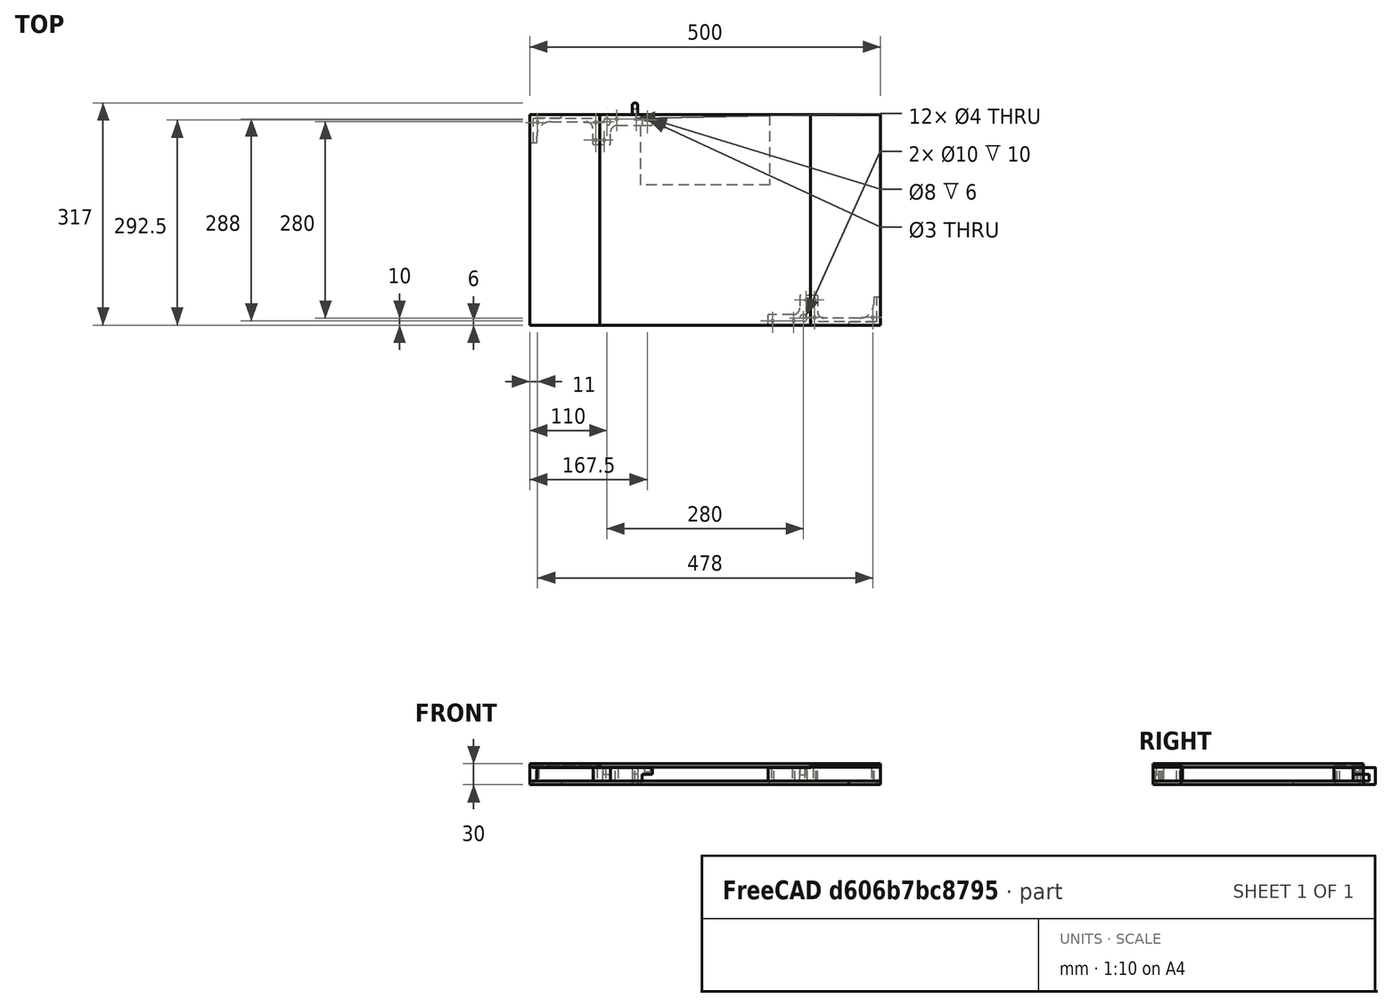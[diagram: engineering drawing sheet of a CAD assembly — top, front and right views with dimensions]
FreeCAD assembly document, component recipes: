
FREECAD ASSEMBLY — COMPONENT RECIPES ("ChessBoard")

This assembly document has 9 components, labeled P0..P8 below (a component is one placed body or linked part). 6 of them carry a construction recipe — the FreeCAD feature program that regenerates the part from scratch, quoted from this document or its linked companion documents; the rest are supplied as boundary geometry only. No exploded tour is included for this assembly.
COMPONENT P0 — recipe-attached ("Bottom", modeled in this document).
Construction recipe (the document's own serialized feature program — sketch geometry with constraints, then the solid features built on it; lengths are millimeters unless a unit is written):

FEATURE [Sketcher::SketchObject] Sketch
  ArcFitTolerance = 1e-06
  AttachmentSupport = -> [XY_Plane]
  FullyConstrained = true
  MakeInternals = false
  MapMode = 5
  sketch-geometry (5):
    g0: LineSegment StartX=-250 StartY=-150 StartZ=0 EndX=250 EndY=-150 EndZ=0
    g1: LineSegment StartX=250 StartY=-150 StartZ=0 EndX=250 EndY=150 EndZ=0
    g2: LineSegment StartX=250 StartY=150 StartZ=0 EndX=-250 EndY=150 EndZ=0
    g3: LineSegment StartX=-250 StartY=150 StartZ=0 EndX=-250 EndY=-150 EndZ=0
    g4: GeomPoint [constr] X=0 Y=0 Z=0
  constraints (12):
    c: Coincident(g0,g1)
    c: Coincident(g1,g2)
    c: Coincident(g2,g3)
    c: Coincident(g3,g0)
    c: Horizontal(g0)
    c: Horizontal(g2)
    c: Vertical(g1)
    c: Vertical(g3)
    c: Symmetric(g2,g0,g4)
    c: Distance(g1,g3) = 500
    c: Distance(g0,g2) = 300
    c: Coincident(g4,g-1)
FEATURE [PartDesign::Pad] Pad
  Direction = (0,0,1)
  Length = 5
  Length2 = 10
  Profile = -> Sketch
  ReferenceAxis = -> Sketch [N_Axis]
  Refine = true
  Suppressed = false
  Type = 0
FEATURE [Sketcher::SketchObject] Sketch005
  ArcFitTolerance = 1e-06
  AttachmentSupport = -> [Pad]
  ExternalGeometry = -> [Sketch]
  FullyConstrained = false
  MakeInternals = false
  MapMode = 5
  Placement = pos=(0,0,0) rot=(1,0,0;3.14159rad)
  sketch-geometry (4):
    g0: LineSegment StartX=-92 StartY=-50 StartZ=0 EndX=-92 EndY=-193.39 EndZ=0
    g1: LineSegment StartX=-92 StartY=-193.39 StartZ=0 EndX=92 EndY=-193.39 EndZ=0
    g2: LineSegment StartX=92 StartY=-193.39 StartZ=0 EndX=92 EndY=-50 EndZ=0
    g3: LineSegment StartX=92 StartY=-50 StartZ=0 EndX=-92 EndY=-50 EndZ=0
  constraints (11):
    c: Coincident(g0,g1)
    c: Coincident(g1,g2)
    c: Coincident(g2,g3)
    c: Coincident(g3,g0)
    c: Vertical(g0)
    c: Vertical(g2)
    c: Horizontal(g1)
    c: Horizontal(g3)
    c: Distance(g-2,g2) = 92
    c: Distance(g-2,g0) = 92
    c: Distance(g-3,g3) = 100
FEATURE [PartDesign::Pocket] Pocket
  BaseFeature = -> Pad
  Direction = (0,0,1)
  Length = 5
  Length2 = 5
  Profile = -> Sketch005
  ReferenceAxis = -> Sketch005 [N_Axis]
  Refine = true
  Suppressed = false
  Type = 0
FEATURE [PartDesign::Body] Body  label="Bottom"
  AllowCompound = false
  Group = -> [Sketch,Pad,Sketch005,Pocket]
  Origin = -> Origin
  Tip = -> Pocket
COMPONENT P1 — recipe-attached ("MainBoard", modeled in this document).
Construction recipe (the document's own serialized feature program — sketch geometry with constraints, then the solid features built on it; lengths are millimeters unless a unit is written):

FEATURE [Sketcher::SketchObject] Sketch001
  ArcFitTolerance = 1e-06
  AttachmentSupport = -> [XY_Plane001]
  FullyConstrained = true
  MakeInternals = false
  MapMode = 5
  sketch-geometry (5):
    g0: LineSegment StartX=-150 StartY=-150 StartZ=0 EndX=150 EndY=-150 EndZ=0
    g1: LineSegment StartX=150 StartY=-150 StartZ=0 EndX=150 EndY=150 EndZ=0
    g2: LineSegment StartX=150 StartY=150 StartZ=0 EndX=-150 EndY=150 EndZ=0
    g3: LineSegment StartX=-150 StartY=150 StartZ=0 EndX=-150 EndY=-150 EndZ=0
    g4: GeomPoint [constr] X=0 Y=0 Z=0
  constraints (12):
    c: Coincident(g0,g1)
    c: Coincident(g1,g2)
    c: Coincident(g2,g3)
    c: Coincident(g3,g0)
    c: Horizontal(g0)
    c: Horizontal(g2)
    c: Vertical(g1)
    c: Vertical(g3)
    c: Symmetric(g2,g0,g4)
    c: Distance(g1,g3) = 300
    c: Distance(g0,g2) = 300
    c: Coincident(g4,g-1)
FEATURE [PartDesign::Pad] Pad001
  Direction = (0,0,1)
  Length = 5
  Length2 = 10
  Profile = -> Sketch001
  ReferenceAxis = -> Sketch001 [N_Axis]
  Refine = true
  Suppressed = false
  Type = 0
FEATURE [PartDesign::Body] Body001  label="MainBoard"
  AllowCompound = false
  Group = -> [Sketch001,Pad001]
  Origin = -> Origin001
  Placement = pos=(0,0,25) rot=(0,0,1;0rad)
  Tip = -> Pad001
COMPONENT P2 — recipe-attached ("DropLeft", modeled in this document).
Construction recipe (the document's own serialized feature program — sketch geometry with constraints, then the solid features built on it; lengths are millimeters unless a unit is written):

FEATURE [Sketcher::SketchObject] Sketch002
  ArcFitTolerance = 1e-06
  AttachmentSupport = -> [XY_Plane002]
  FullyConstrained = true
  MakeInternals = false
  MapMode = 5
  sketch-geometry (4):
    g0: LineSegment StartX=0 StartY=0 StartZ=0 EndX=0 EndY=-300 EndZ=0
    g1: LineSegment StartX=0 StartY=-300 StartZ=0 EndX=100 EndY=-300 EndZ=0
    g2: LineSegment StartX=100 StartY=-300 StartZ=0 EndX=100 EndY=0 EndZ=0
    g3: LineSegment StartX=100 StartY=0 StartZ=0 EndX=0 EndY=0 EndZ=0
  constraints (11):
    c: Coincident(g0,g1)
    c: Coincident(g1,g2)
    c: Coincident(g2,g3)
    c: Coincident(g3,g0)
    c: Vertical(g0)
    c: Vertical(g2)
    c: Horizontal(g1)
    c: Horizontal(g3)
    c: Distance(g0,g2) = 100
    c: Distance(g1,g3) = 300
    c: Coincident(g0,g-1)
FEATURE [PartDesign::Pad] Pad002
  Direction = (0,0,1)
  Length = 5
  Length2 = 10
  Profile = -> Sketch002
  ReferenceAxis = -> Sketch002 [N_Axis]
  Refine = true
  Suppressed = false
  Type = 0
FEATURE [PartDesign::Body] Body002  label="DropLeft"
  AllowCompound = false
  Group = -> [Sketch002,Pad002]
  Origin = -> Origin002
  Placement = pos=(-250,150,25) rot=(0,0,1;0rad)
  Tip = -> Pad002
COMPONENT P3 — recipe-attached ("DropRight", modeled in this document).
Construction recipe (the document's own serialized feature program — sketch geometry with constraints, then the solid features built on it; lengths are millimeters unless a unit is written):

FEATURE [Sketcher::SketchObject] Sketch003
  ArcFitTolerance = 1e-06
  AttachmentSupport = -> [XY_Plane003]
  FullyConstrained = true
  MakeInternals = false
  MapMode = 5
  sketch-geometry (4):
    g0: LineSegment StartX=0 StartY=0 StartZ=0 EndX=-100 EndY=0 EndZ=0
    g1: LineSegment StartX=-100 StartY=0 StartZ=0 EndX=-100 EndY=-300 EndZ=0
    g2: LineSegment StartX=-100 StartY=-300 StartZ=0 EndX=0 EndY=-300 EndZ=0
    g3: LineSegment StartX=0 StartY=-300 StartZ=0 EndX=0 EndY=0 EndZ=0
  constraints (11):
    c: Coincident(g0,g1)
    c: Coincident(g1,g2)
    c: Coincident(g2,g3)
    c: Coincident(g3,g0)
    c: Horizontal(g0)
    c: Horizontal(g2)
    c: Vertical(g1)
    c: Vertical(g3)
    c: Distance(g1,g3) = 100
    c: Distance(g0,g2) = 300
    c: Coincident(g0,g-1)
FEATURE [PartDesign::Pad] Pad003
  Direction = (0,0,1)
  Length = 5
  Length2 = 10
  Profile = -> Sketch003
  ReferenceAxis = -> Sketch003 [N_Axis]
  Refine = true
  Suppressed = false
  Type = 0
FEATURE [PartDesign::Body] Body003  label="DropRight"
  AllowCompound = false
  Group = -> [Sketch003,Pad003]
  Origin = -> Origin003
  Placement = pos=(250,150,25) rot=(0,0,1;0rad)
  Tip = -> Pad003
COMPONENT P4 — recipe-attached ("AnchorBL", modeled in this document).
Construction recipe (the document's own serialized feature program — sketch geometry with constraints, then the solid features built on it; lengths are millimeters unless a unit is written):

FEATURE [Sketcher::SketchObject] Sketch004
  ArcFitTolerance = 1e-06
  AttachmentSupport = -> [XY_Plane004]
  FullyConstrained = false
  MakeInternals = false
  MapMode = 5
  sketch-geometry (13):
    g0: LineSegment StartX=0 StartY=40 StartZ=0 EndX=0 EndY=0 EndZ=0
    g1: LineSegment StartX=0 StartY=0 StartZ=0 EndX=160 EndY=0 EndZ=0
    g2: LineSegment StartX=0 StartY=40 StartZ=0 EndX=10 EndY=40 EndZ=0
    g3: LineSegment StartX=10 StartY=40 StartZ=0 EndX=10 EndY=30 EndZ=0
    g4: ArcOfCircle CenterX=30 CenterY=30 CenterZ=0 NormalX=0 NormalY=0 NormalZ=1 AngleXU=0 Radius=20 StartAngle=3.14159 EndAngle=4.71239
    g5: LineSegment StartX=90 StartY=42.0946 StartZ=0 EndX=115 EndY=42.0946 EndZ=0
    g6: LineSegment StartX=115 StartY=42.0946 StartZ=0 EndX=115 EndY=25 EndZ=0
    g7: LineSegment StartX=90 StartY=42.0946 StartZ=0 EndX=90 EndY=20 EndZ=0
    g8: LineSegment StartX=30 StartY=10 StartZ=0 EndX=80 EndY=10 EndZ=0
    g9: ArcOfCircle CenterX=125 CenterY=25 CenterZ=0 NormalX=0 NormalY=0 NormalZ=1 AngleXU=0 Radius=10 StartAngle=3.14159 EndAngle=4.71239
    g10: ArcOfCircle CenterX=80 CenterY=20 CenterZ=0 NormalX=0 NormalY=0 NormalZ=1 AngleXU=0 Radius=10 StartAngle=4.71239 EndAngle=6.28319
    g11: LineSegment StartX=125 StartY=15 StartZ=0 EndX=160 EndY=15 EndZ=0
    g12: LineSegment StartX=160 StartY=15 StartZ=0 EndX=160 EndY=0 EndZ=0
  constraints (38):
    c: PointOnObject(g0,g-2)
    c: Coincident(g0,g-1)
    c: Coincident(g0,g1)
    c: Coincident(g0,g2)
    c: Horizontal(g2)
    c: Coincident(g2,g3)
    c: Vertical(g3)
    c: Coincident(g4,g3)
    c: Vertical(g4,g4)
    c: Horizontal(g4,g3)
    c: Radius(g4) = 20
    c: DistanceY(g1,g9) = 15
    c: Distance(g2,g2) = 10
    c: DistanceY(g0,g0) = 40
    c: Horizontal(g5)
    c: Coincident(g5,g6)
    c: Vertical(g6)
    c: Coincident(g5,g7)
    c: Vertical(g7)
    c: Tangent(g4,g8) = -1.5708
    c: Coincident(g9,g6)
    c: Coincident(g10,g7)
    c: Coincident(g10,g8)
    c: Distance(g1,g8) = 10
    c: Radius(g10) = 10
    c: Vertical(g10,g8)
    c: Horizontal(g10,g7)
    c: Radius(g9) = 10
    c: Vertical(g9,g9)
    c: Horizontal(g9,g6)
    c: DistanceX(g-1,g10) = 80
    c: Tangent(g9,g11) = -1.5708
    c: Coincident(g11,g12)
    c: Vertical(g12)
    c: Coincident(g1,g12)
    c: Horizontal(g1)
    c: Distance(g-2,g12) = 160
    c: DistanceX(g5,g5) = 25
FEATURE [PartDesign::Pad] Pad004
  Direction = (0,0,1)
  Length = 29
  Length2 = 10
  Profile = -> Sketch004
  ReferenceAxis = -> Sketch004 [N_Axis]
  Refine = true
  Suppressed = false
  Type = 0
FEATURE [Sketcher::SketchObject] Sketch006
  ArcFitTolerance = 1e-06
  AttachmentSupport = -> [Pad004]
  FullyConstrained = false
  MakeInternals = false
  MapMode = 5
  Placement = pos=(0,0,29) rot=(0,0,1;0rad)
  sketch-geometry (6):
    g0: LineSegment StartX=5 StartY=45 StartZ=0 EndX=5 EndY=5 EndZ=0
    g1: LineSegment StartX=5 StartY=5 StartZ=0 EndX=100 EndY=5 EndZ=0
    g2: LineSegment StartX=275.375 StartY=45 StartZ=0 EndX=5 EndY=45 EndZ=0
    g3: LineSegment StartX=100 StartY=5 StartZ=0 EndX=100 EndY=-8.02974 EndZ=0
    g4: LineSegment StartX=100 StartY=-8.02974 StartZ=0 EndX=275.375 EndY=-8.02974 EndZ=0
    g5: LineSegment StartX=275.375 StartY=45 StartZ=0 EndX=275.375 EndY=-8.02974 EndZ=0
  constraints (16):
    c: Coincident(g0,g1)
    c: Coincident(g2,g0)
    c: Vertical(g0)
    c: Horizontal(g1)
    c: Horizontal(g2)
    c: Distance(g-2,g0) = 5
    c: Distance(g-1,g1) = 5
    c: DistanceY(g0,g0) = 40
    c: Vertical(g3)
    c: Coincident(g3,g4)
    c: Horizontal(g4)
    c: Coincident(g1,g3)
    c: Coincident(g5,g2)
    c: Coincident(g5,g4)
    c: Vertical(g5)
    c: Distance(g-2,g3) = 100
FEATURE [PartDesign::Pocket] Pocket001
  BaseFeature = -> Pad004
  Direction = (0,0,-1)
  Length = 5
  Length2 = 5
  Profile = -> Sketch006
  ReferenceAxis = -> Sketch006 [N_Axis]
  Refine = true
  Suppressed = false
  Type = 0
FEATURE [Sketcher::SketchObject] Sketch007
  ArcFitTolerance = 1e-06
  AttachmentSupport = -> [Pocket001]
  FullyConstrained = false
  MakeInternals = false
  MapMode = 5
  Placement = pos=(0,0,0) rot=(1,0,0;3.14159rad)
  sketch-geometry (6):
    g0: LineSegment StartX=5 StartY=-5 StartZ=0 EndX=5 EndY=-45 EndZ=0
    g1: LineSegment StartX=5 StartY=-45 StartZ=0 EndX=160 EndY=-45 EndZ=0
    g2: LineSegment StartX=45 StartY=-5 StartZ=0 EndX=5 EndY=-5 EndZ=0
    g3: LineSegment StartX=45 StartY=-5 StartZ=0 EndX=45 EndY=8.54607 EndZ=0
    g4: LineSegment StartX=45 StartY=8.54607 StartZ=0 EndX=160 EndY=8.54607 EndZ=0
    g5: LineSegment StartX=160 StartY=8.54607 StartZ=0 EndX=160 EndY=-45 EndZ=0
  constraints (17):
    c: Coincident(g0,g1)
    c: Coincident(g2,g0)
    c: Vertical(g0)
    c: Horizontal(g1)
    c: Horizontal(g2)
    c: Distance(g-1,g2) = 5
    c: Distance(g-2,g0) = 5
    c: DistanceY(g0,g0) = 40
    c: Coincident(g2,g3)
    c: Vertical(g3)
    c: Coincident(g3,g4)
    c: Horizontal(g4)
    c: Coincident(g4,g5)
    c: Coincident(g5,g1)
    c: Vertical(g5)
    c: DistanceX(g0,g2) = 40
    c: Distance(g1,g-2) = 160
FEATURE [PartDesign::Pocket] Pocket002
  BaseFeature = -> Pocket001
  Direction = (0,0,1)
  Length = 5
  Length2 = 5
  Profile = -> Sketch007
  ReferenceAxis = -> Sketch007 [N_Axis]
  Refine = true
  Suppressed = false
  Type = 0
FEATURE [Sketcher::SketchObject] Sketch008
  ArcFitTolerance = 1e-06
  AttachmentSupport = -> [Pocket002]
  ExternalGeometry = -> [Pocket002]
  FullyConstrained = true
  MakeInternals = false
  MapMode = 5
  Placement = pos=(0,0,24) rot=(0,0,1;0rad)
  sketch-geometry (1):
    g0: Circle CenterX=110 CenterY=10 CenterZ=0 NormalX=0 NormalY=0 NormalZ=1 AngleXU=0 Radius=5
  constraints (3):
    c: Diameter(g0) = 10
    c: Distance(g0,g-1) = 10
    c: DistanceX(g-3,g0) = 10
FEATURE [PartDesign::Pocket] Pocket003
  BaseFeature = -> Pocket002
  Direction = (0,0,-1)
  Length = 10
  Length2 = 5
  Profile = -> Sketch008
  ReferenceAxis = -> Sketch008 [N_Axis]
  Refine = true
  Suppressed = false
  Type = 0
FEATURE [Sketcher::SketchObject] Sketch015
  ArcFitTolerance = 1e-06
  AttachmentSupport = -> [Pocket003]
  ExternalGeometry = -> [Pocket003]
  FullyConstrained = true
  MakeInternals = false
  MapMode = 5
  Placement = pos=(0,0,24) rot=(0,0,1;0rad)
  sketch-geometry (6):
    g0: Circle CenterX=11 CenterY=11 CenterZ=0 NormalX=0 NormalY=0 NormalZ=1 AngleXU=0 Radius=2
    g1: Circle CenterX=94 CenterY=11 CenterZ=0 NormalX=0 NormalY=0 NormalZ=1 AngleXU=0 Radius=2
    g2: Circle CenterX=94 CenterY=36 CenterZ=0 NormalX=0 NormalY=0 NormalZ=1 AngleXU=0 Radius=2
    g3: Circle CenterX=106 CenterY=36 CenterZ=0 NormalX=0 NormalY=0 NormalZ=1 AngleXU=0 Radius=2
    g4: Circle CenterX=124 CenterY=6 CenterZ=0 NormalX=0 NormalY=0 NormalZ=1 AngleXU=0 Radius=2
    g5: Circle CenterX=154 CenterY=6 CenterZ=0 NormalX=0 NormalY=0 NormalZ=1 AngleXU=0 Radius=2
  constraints (18):
    c: Diameter(g0) = 4
    c: Diameter(g1) = 4
    c: Diameter(g2) = 4
    c: Distance(g1,g-3) = 6
    c: Vertical(g2,g1)
    c: Distance(g1,g-5) = 6
    c: DistanceY(g1,g2) = 25
    c: Distance(g0,g-5) = 6
    c: Distance(g0,g-4) = 6
    c: Diameter(g3) = 4
    c: Diameter(g4) = 4
    c: Horizontal(g3,g2)
    c: Distance(g3,g-3) = 6
    c: Distance(g4,g-1) = 6
    c: Distance(g4,g-3) = 24
    c: Diameter(g5) = 4
    c: Distance(g5,g-1) = 6
    c: Distance(g5,g-6) = 6
FEATURE [PartDesign::Pocket] Pocket007
  BaseFeature = -> Pocket003
  Direction = (0,0,-1)
  Length = 5
  Length2 = 5
  Profile = -> Sketch015
  ReferenceAxis = -> Sketch015 [N_Axis]
  Refine = true
  Suppressed = false
  Type = 1
FEATURE [PartDesign::Body] Body004  label="AnchorBL"
  AllowCompound = false
  Group = -> [Sketch004,Pad004,Sketch006,Pocket001,Sketch007,Pocket002,Sketch008,Pocket003,Sketch015,Pocket007]
  Origin = -> Origin004
  Placement = pos=(-250,-150,0) rot=(0,0,1;0rad)
  Tip = -> Pocket007
COMPONENT P5 — recipe-attached ("AnchorTR", modeled in this document).
Construction recipe (the document's own serialized feature program — sketch geometry with constraints, then the solid features built on it; lengths are millimeters unless a unit is written):

FEATURE [Sketcher::SketchObject] Sketch009
  ArcFitTolerance = 1e-06
  AttachmentSupport = -> [XY_Plane005]
  FullyConstrained = false
  MakeInternals = false
  MapMode = 5
  sketch-geometry (13):
    g0: LineSegment StartX=0 StartY=40 StartZ=0 EndX=0 EndY=0 EndZ=0
    g1: LineSegment StartX=0 StartY=0 StartZ=0 EndX=160 EndY=0 EndZ=0
    g2: LineSegment StartX=0 StartY=40 StartZ=0 EndX=10 EndY=40 EndZ=0
    g3: LineSegment StartX=10 StartY=40 StartZ=0 EndX=10 EndY=30 EndZ=0
    g4: ArcOfCircle CenterX=30 CenterY=30 CenterZ=0 NormalX=0 NormalY=0 NormalZ=1 AngleXU=0 Radius=20 StartAngle=3.14159 EndAngle=4.71239
    g5: LineSegment StartX=90 StartY=42.0946 StartZ=0 EndX=115 EndY=42.0946 EndZ=0
    g6: LineSegment StartX=115 StartY=42.0946 StartZ=0 EndX=115 EndY=25 EndZ=0
    g7: LineSegment StartX=90 StartY=42.0946 StartZ=0 EndX=90 EndY=20 EndZ=0
    g8: LineSegment StartX=30 StartY=10 StartZ=0 EndX=80 EndY=10 EndZ=0
    g9: ArcOfCircle CenterX=125 CenterY=25 CenterZ=0 NormalX=0 NormalY=0 NormalZ=1 AngleXU=0 Radius=10 StartAngle=3.14159 EndAngle=4.71239
    g10: ArcOfCircle CenterX=80 CenterY=20 CenterZ=0 NormalX=0 NormalY=0 NormalZ=1 AngleXU=0 Radius=10 StartAngle=4.71239 EndAngle=6.28319
    g11: LineSegment StartX=125 StartY=15 StartZ=0 EndX=160 EndY=15 EndZ=0
    g12: LineSegment StartX=160 StartY=15 StartZ=0 EndX=160 EndY=0 EndZ=0
  constraints (38):
    c: PointOnObject(g0,g-2)
    c: Coincident(g0,g-1)
    c: Coincident(g0,g1)
    c: Coincident(g0,g2)
    c: Horizontal(g2)
    c: Coincident(g2,g3)
    c: Vertical(g3)
    c: Coincident(g4,g3)
    c: Vertical(g4,g4)
    c: Horizontal(g4,g3)
    c: Radius(g4) = 20
    c: DistanceY(g1,g9) = 15
    c: Distance(g2,g2) = 10
    c: DistanceY(g0,g0) = 40
    c: Horizontal(g5)
    c: Coincident(g5,g6)
    c: Vertical(g6)
    c: Coincident(g5,g7)
    c: Vertical(g7)
    c: Tangent(g4,g8) = -1.5708
    c: Coincident(g9,g6)
    c: Coincident(g10,g7)
    c: Coincident(g10,g8)
    c: Distance(g1,g8) = 10
    c: Radius(g10) = 10
    c: Vertical(g10,g8)
    c: Horizontal(g10,g7)
    c: Radius(g9) = 10
    c: Vertical(g9,g9)
    c: Horizontal(g9,g6)
    c: DistanceX(g-1,g10) = 80
    c: Tangent(g9,g11) = -1.5708
    c: Coincident(g11,g12)
    c: Vertical(g12)
    c: Coincident(g1,g12)
    c: Horizontal(g1)
    c: Distance(g-2,g12) = 160
    c: DistanceX(g5,g5) = 25
FEATURE [PartDesign::Pad] Pad005
  Direction = (0,0,1)
  Length = 29
  Length2 = 10
  Profile = -> Sketch009
  ReferenceAxis = -> Sketch009 [N_Axis]
  Refine = true
  Suppressed = false
  Type = 0
FEATURE [Sketcher::SketchObject] Sketch010
  ArcFitTolerance = 1e-06
  AttachmentSupport = -> [Pad005]
  FullyConstrained = false
  MakeInternals = false
  MapMode = 5
  Placement = pos=(0,0,29) rot=(0,0,1;0rad)
  sketch-geometry (6):
    g0: LineSegment StartX=5 StartY=45 StartZ=0 EndX=5 EndY=5 EndZ=0
    g1: LineSegment StartX=5 StartY=5 StartZ=0 EndX=100 EndY=5 EndZ=0
    g2: LineSegment StartX=275.375 StartY=45 StartZ=0 EndX=5 EndY=45 EndZ=0
    g3: LineSegment StartX=100 StartY=5 StartZ=0 EndX=100 EndY=-8.02974 EndZ=0
    g4: LineSegment StartX=100 StartY=-8.02974 StartZ=0 EndX=275.375 EndY=-8.02974 EndZ=0
    g5: LineSegment StartX=275.375 StartY=45 StartZ=0 EndX=275.375 EndY=-8.02974 EndZ=0
  constraints (16):
    c: Coincident(g0,g1)
    c: Coincident(g2,g0)
    c: Vertical(g0)
    c: Horizontal(g1)
    c: Horizontal(g2)
    c: Distance(g-2,g0) = 5
    c: Distance(g-1,g1) = 5
    c: DistanceY(g0,g0) = 40
    c: Vertical(g3)
    c: Coincident(g3,g4)
    c: Horizontal(g4)
    c: Coincident(g1,g3)
    c: Coincident(g5,g2)
    c: Coincident(g5,g4)
    c: Vertical(g5)
    c: Distance(g-2,g3) = 100
FEATURE [PartDesign::Pocket] Pocket004
  BaseFeature = -> Pad005
  Direction = (0,0,-1)
  Length = 5
  Length2 = 5
  Profile = -> Sketch010
  ReferenceAxis = -> Sketch010 [N_Axis]
  Refine = true
  Suppressed = false
  Type = 0
FEATURE [Sketcher::SketchObject] Sketch011
  ArcFitTolerance = 1e-06
  AttachmentSupport = -> [Pocket004]
  FullyConstrained = false
  MakeInternals = false
  MapMode = 5
  Placement = pos=(0,0,0) rot=(1,0,0;3.14159rad)
  sketch-geometry (6):
    g0: LineSegment StartX=5 StartY=-5 StartZ=0 EndX=5 EndY=-45 EndZ=0
    g1: LineSegment StartX=5 StartY=-45 StartZ=0 EndX=160 EndY=-45 EndZ=0
    g2: LineSegment StartX=45 StartY=-5 StartZ=0 EndX=5 EndY=-5 EndZ=0
    g3: LineSegment StartX=45 StartY=-5 StartZ=0 EndX=45 EndY=8.54607 EndZ=0
    g4: LineSegment StartX=45 StartY=8.54607 StartZ=0 EndX=160 EndY=8.54607 EndZ=0
    g5: LineSegment StartX=160 StartY=8.54607 StartZ=0 EndX=160 EndY=-45 EndZ=0
  constraints (17):
    c: Coincident(g0,g1)
    c: Coincident(g2,g0)
    c: Vertical(g0)
    c: Horizontal(g1)
    c: Horizontal(g2)
    c: Distance(g-1,g2) = 5
    c: Distance(g-2,g0) = 5
    c: DistanceY(g0,g0) = 40
    c: Coincident(g2,g3)
    c: Vertical(g3)
    c: Coincident(g3,g4)
    c: Horizontal(g4)
    c: Coincident(g4,g5)
    c: Coincident(g5,g1)
    c: Vertical(g5)
    c: DistanceX(g0,g2) = 40
    c: Distance(g1,g-2) = 160
FEATURE [PartDesign::Pocket] Pocket005
  BaseFeature = -> Pocket004
  Direction = (0,0,1)
  Length = 5
  Length2 = 5
  Profile = -> Sketch011
  ReferenceAxis = -> Sketch011 [N_Axis]
  Refine = true
  Suppressed = false
  Type = 0
FEATURE [Sketcher::SketchObject] Sketch012
  ArcFitTolerance = 1e-06
  AttachmentSupport = -> [Pocket005]
  ExternalGeometry = -> [Pocket005]
  FullyConstrained = true
  MakeInternals = false
  MapMode = 5
  Placement = pos=(0,0,24) rot=(0,0,1;0rad)
  sketch-geometry (1):
    g0: Circle CenterX=110 CenterY=10 CenterZ=0 NormalX=0 NormalY=0 NormalZ=1 AngleXU=0 Radius=5
  constraints (3):
    c: Diameter(g0) = 10
    c: Distance(g0,g-1) = 10
    c: DistanceX(g-3,g0) = 10
FEATURE [PartDesign::Pocket] Pocket006
  BaseFeature = -> Pocket005
  Direction = (0,0,-1)
  Length = 10
  Length2 = 5
  Profile = -> Sketch012
  ReferenceAxis = -> Sketch012 [N_Axis]
  Refine = true
  Suppressed = false
  Type = 0
FEATURE [Sketcher::SketchObject] Sketch013
  ArcFitTolerance = 1e-06
  AttachmentSupport = -> [Pocket006]
  ExternalGeometry = -> [Pocket006]
  FullyConstrained = true
  MakeInternals = false
  MapMode = 5
  Placement = pos=(160,0,0) rot=(0.57735,0.57735,0.57735;2.0944rad)
  sketch-geometry (4):
    g0: LineSegment StartX=15 StartY=24 StartZ=0 EndX=0 EndY=24 EndZ=0
    g1: LineSegment StartX=0 StartY=24 StartZ=0 EndX=0 EndY=15 EndZ=0
    g2: LineSegment StartX=0 StartY=15 StartZ=0 EndX=15 EndY=15 EndZ=0
    g3: LineSegment StartX=15 StartY=15 StartZ=0 EndX=15 EndY=24 EndZ=0
  constraints (11):
    c: Coincident(g0,g1)
    c: Coincident(g1,g2)
    c: Coincident(g2,g3)
    c: Coincident(g3,g0)
    c: Horizontal(g0)
    c: Horizontal(g2)
    c: Vertical(g1)
    c: Vertical(g3)
    c: Coincident(g0,g-3)
    c: PointOnObject(g1,g-2)
    c: Distance(g-1,g2) = 15
FEATURE [PartDesign::Pad] Pad006
  BaseFeature = -> Pocket006
  Direction = (1,0,0)
  Length = 15
  Length2 = 10
  Profile = -> Sketch013
  ReferenceAxis = -> Sketch013 [N_Axis]
  Refine = true
  Suppressed = false
  Type = 0
FEATURE [Sketcher::SketchObject] Sketch014
  ArcFitTolerance = 1e-06
  AttachmentSupport = -> [Pad006]
  ExternalGeometry = -> [Pad006]
  FullyConstrained = true
  MakeInternals = false
  MapMode = 5
  Placement = pos=(0,0,24) rot=(0,0,1;0rad)
  sketch-geometry (1):
    g0: Circle CenterX=167.5 CenterY=7.5 CenterZ=0 NormalX=0 NormalY=0 NormalZ=1 AngleXU=0 Radius=1.75
  constraints (2):
    c: Diameter(g0) = 3.5
    c: Symmetric(g-3,g-4,g0)
FEATURE [PartDesign::Hole] Hole
  BaseFeature = -> Pad006
  CustomThreadClearance = 0
  Depth = 25
  DepthType = 0
  Diameter = 3
  DrillForDepth = false
  DrillPoint = 1
  DrillPointAngle = 118
  HoleCutCountersinkAngle = 90
  HoleCutCustomValues = false
  HoleCutDepth = 0
  HoleCutDiameter = 6.1
  HoleCutType = 0
  ModelThread = false
  Profile = -> Sketch014
  Refine = true
  Suppressed = false
  Tapered = false
  TaperedAngle = 90
  ThreadClass = 0
  ThreadDepth = 25
  ThreadDepthType = 0
  ThreadDirection = 0
  ThreadFit = 0
  ThreadSize = 0
  ThreadType = 0
  Threaded = false
  UseCustomThreadClearance = false
FEATURE [PartDesign::Hole] Hole001
  BaseFeature = -> Hole
  CustomThreadClearance = 0
  Depth = 6
  DepthType = 0
  Diameter = 8
  DrillForDepth = false
  DrillPoint = 0
  DrillPointAngle = 118
  HoleCutCountersinkAngle = 90
  HoleCutCustomValues = false
  HoleCutDepth = 0
  HoleCutDiameter = 6.1
  HoleCutType = 0
  ModelThread = false
  Profile = -> Sketch014
  Refine = true
  Suppressed = false
  Tapered = false
  TaperedAngle = 90
  ThreadClass = 0
  ThreadDepth = 6
  ThreadDepthType = 0
  ThreadDirection = 0
  ThreadFit = 0
  ThreadSize = 0
  ThreadType = 0
  Threaded = false
  UseCustomThreadClearance = false
FEATURE [Sketcher::SketchObject] Sketch016
  ArcFitTolerance = 1e-06
  AttachmentSupport = -> [Hole001]
  ExternalGeometry = -> [Hole001]
  FullyConstrained = true
  MakeInternals = false
  MapMode = 5
  Placement = pos=(0,0,24) rot=(0,0,1;0rad)
  sketch-geometry (6):
    g0: Circle CenterX=11 CenterY=11 CenterZ=0 NormalX=0 NormalY=0 NormalZ=1 AngleXU=0 Radius=2
    g1: Circle CenterX=94 CenterY=11 CenterZ=0 NormalX=0 NormalY=0 NormalZ=1 AngleXU=0 Radius=2
    g2: Circle CenterX=94 CenterY=36 CenterZ=0 NormalX=0 NormalY=0 NormalZ=1 AngleXU=0 Radius=2
    g3: Circle CenterX=106 CenterY=36 CenterZ=0 NormalX=0 NormalY=0 NormalZ=1 AngleXU=0 Radius=2
    g4: Circle CenterX=124 CenterY=6 CenterZ=0 NormalX=0 NormalY=0 NormalZ=1 AngleXU=0 Radius=2
    g5: Circle CenterX=152 CenterY=6 CenterZ=0 NormalX=0 NormalY=0 NormalZ=1 AngleXU=0 Radius=2
  constraints (18):
    c: Diameter(g0) = 4
    c: Diameter(g1) = 4
    c: Diameter(g2) = 4
    c: Diameter(g3) = 4
    c: Diameter(g4) = 4
    c: Diameter(g5) = 4
    c: Distance(g0,g-3) = 6
    c: Distance(g0,g-4) = 6
    c: DistanceX(g1,g-4) = 6
    c: Distance(g1,g-4) = 6
    c: Vertical(g1,g2)
    c: Horizontal(g3,g2)
    c: DistanceX(g-4,g3) = 6
    c: Distance(g4,g-1) = 6
    c: DistanceX(g-4,g4) = 24
    c: Horizontal(g5,g4)
    c: Distance(g5,g-5) = 8
    c: DistanceY(g1,g2) = 25
FEATURE [PartDesign::Pocket] Pocket008
  BaseFeature = -> Hole001
  Direction = (0,0,-1)
  Length = 5
  Length2 = 5
  Profile = -> Sketch016
  ReferenceAxis = -> Sketch016 [N_Axis]
  Refine = true
  Suppressed = false
  Type = 1
FEATURE [Sketcher::SketchObject] Sketch017
  ArcFitTolerance = 1e-06
  AttachmentSupport = -> [Pocket008]
  ExternalGeometry = -> [Pocket008]
  FullyConstrained = true
  MakeInternals = false
  MapMode = 5
  Placement = pos=(0,0,24) rot=(0,0,1;0rad)
  sketch-geometry (4):
    g0: LineSegment StartX=146 StartY=0 StartZ=0 EndX=146 EndY=-13 EndZ=0
    g1: ArcOfCircle CenterX=150 CenterY=-13 CenterZ=0 NormalX=0 NormalY=0 NormalZ=1 AngleXU=0 Radius=4 StartAngle=3.14159 EndAngle=6.28319
    g2: LineSegment StartX=154 StartY=-13 StartZ=0 EndX=154 EndY=0 EndZ=0
    g3: LineSegment StartX=146 StartY=0 StartZ=0 EndX=154 EndY=0 EndZ=0
  constraints (12):
    c: Vertical(g0)
    c: Coincident(g1,g0)
    c: Radius(g1) = 4
    c: Tangent(g1,g2) = -1.5708
    c: Vertical(g2)
    c: Coincident(g0,g3)
    c: Coincident(g3,g2)
    c: DistanceY(g1,g-1) = 13
    c: Symmetric(g0,g1,g1)
    c: Distance(g2,g-3) = 6
    c: Horizontal(g3)
    c: Horizontal(g2,g-3)
FEATURE [PartDesign::Pad] Pad007
  BaseFeature = -> Pocket008
  Direction = (0,0,1)
  Length = 24
  Length2 = 10
  Profile = -> Sketch017
  ReferenceAxis = -> Sketch017 [N_Axis]
  Refine = true
  Reversed = true
  Suppressed = false
  Type = 0
FEATURE [Sketcher::SketchObject] Sketch018
  ArcFitTolerance = 1e-06
  AttachmentSupport = -> [Pad007]
  FullyConstrained = true
  MakeInternals = false
  MapMode = 5
  Placement = pos=(154,0,0) rot=(0.57735,0.57735,0.57735;2.0944rad)
  sketch-geometry (4):
    g0: LineSegment StartX=0 StartY=15 StartZ=0 EndX=-8 EndY=15 EndZ=0
    g1: LineSegment StartX=-8 StartY=15 StartZ=0 EndX=-8 EndY=5 EndZ=0
    g2: LineSegment StartX=-8 StartY=5 StartZ=0 EndX=0 EndY=5 EndZ=0
    g3: LineSegment StartX=0 StartY=5 StartZ=0 EndX=0 EndY=15 EndZ=0
  constraints (12):
    c: Coincident(g0,g1)
    c: Coincident(g1,g2)
    c: Coincident(g2,g3)
    c: Coincident(g3,g0)
    c: Horizontal(g0)
    c: Horizontal(g2)
    c: Vertical(g1)
    c: Vertical(g3)
    c: Distance(g1,g3) = 8
    c: Distance(g0,g2) = 10
    c: PointOnObject(g0,g-2)
    c: Distance(g-1,g2) = 5
FEATURE [PartDesign::Pocket] Pocket009
  BaseFeature = -> Pad007
  Direction = (-1,0,0)
  Length = 8
  Length2 = 5
  Profile = -> Sketch018
  ReferenceAxis = -> Sketch018 [N_Axis]
  Refine = true
  Suppressed = false
  Type = 0
FEATURE [PartDesign::Body] Body005  label="AnchorTR"
  AllowCompound = false
  Group = -> [Sketch009,Pad005,Sketch010,Pocket004,Sketch011,Pocket005,Sketch012,Pocket006,Sketch013,Pad006,Sketch014,Hole,Hole001,Sketch016,Pocket008,Sketch017,Pad007,Sketch018,Pocket009]
  Origin = -> Origin005
  Placement = pos=(250,150,0) rot=(0,0,1;3.14159rad)
  Tip = -> Pocket009
COMPONENT P6 — geometry summary ("NavigationBoard"; no construction recipe available for this part):
  bounding box: 187.0 x 64.0 x 30.4 mm
  tessellated surface: 80,282 triangles
  volume: 91933 mm^3 (25% of its bounding box)
  symmetry: mirror-symmetric across its x mid-plane
COMPONENT P7 — geometry summary ("LatchesLock"; no construction recipe available for this part):
  bounding box: 36.0 x 20.0 x 15.0 mm
  tessellated surface: 4,254 triangles
  volume: 7173 mm^3 (66% of its bounding box)
COMPONENT P8 — geometry summary ("LatchesLockRight"; no construction recipe available for this part):
  bounding box: 36.0 x 20.0 x 15.0 mm
  tessellated surface: 4,254 triangles
  volume: 7173 mm^3 (66% of its bounding box)
PROVENANCE & LICENSES
A FreeCAD (.FCStd) document from a public repository crawl; recipes are the document's own serialized feature recipes (and, for linked parts, companion documents' recipes).
License: as declared in the source repository (recorded in the dataset sidecar).
